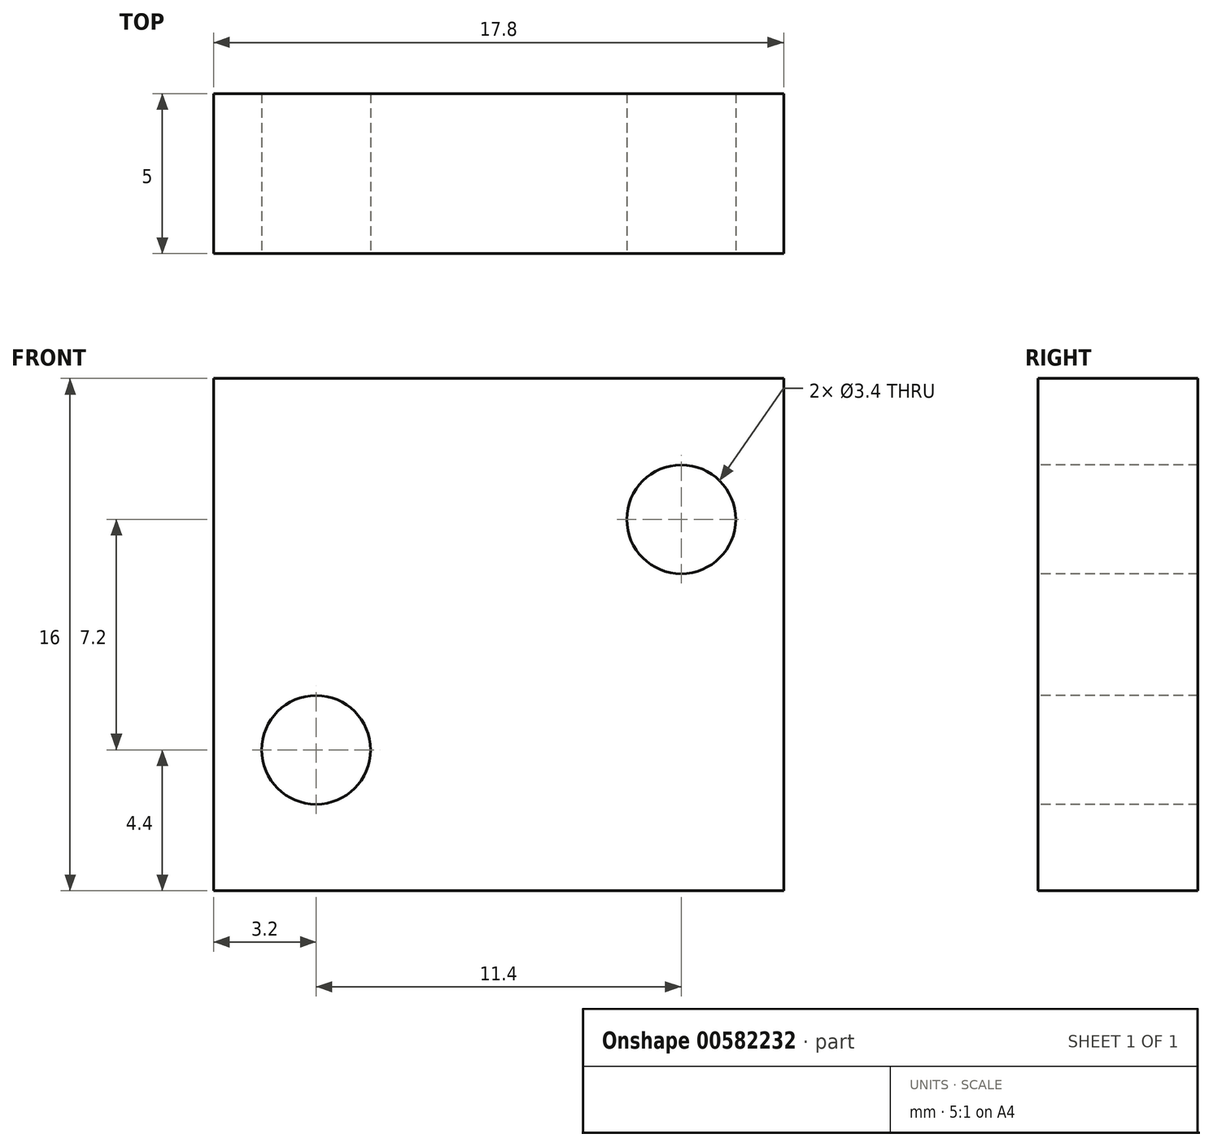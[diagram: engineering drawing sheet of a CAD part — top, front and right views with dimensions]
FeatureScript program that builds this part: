
annotation { "Feature Type Name" : "Feature", "Feature Type Description" : "" }
export const myFeature = defineFeature(function(context is Context, id is Id, definition is map)
    precondition{}
    {
        {
            var Q0;
            Q0=qCreatedBy(makeId("Front.planeOp"),FACE);
            var sketch = newSketch(context, id + "F0", { "sketchPlane" : qUnion([Q0])});
            skLineSegment(sketch, "E0.bottom", {"start": v(0, 0) * mm, "end": v(17.8, 0) * mm});
            skLineSegment(sketch, "E0.top", {"start": v(0, -16) * mm, "end": v(17.8, -16) * mm});
            skLineSegment(sketch, "E0.left", {"start": v(0, 0) * mm, "end": v(0, -16) * mm});
            skLineSegment(sketch, "E0.right", {"start": v(17.8, 0) * mm, "end": v(17.8, -16) * mm});
            skSolve(sketch);
        }
        {
            var Q0;
            Q0=makeQuery(id+"F0.imprint","IMPRINT",FACE,{"disambiguationData":[TD([[makeQuery(id+"F0.imprint","IMPRINT",EDGE,{"derivedFrom":sQuery(id+"F0.wireOp",EDGE,"E0.bottom")}),-1.0]])]});
            extrude(context, id + "F1", {"entities" : qUnion([Q0]), "oppositeDirection" : true, "depth" : 5 * mm, "offsetDistance" : 25 * mm});
        }
        {
            var Q0;
            Q0=makeQuery(id+"F1.opExtrude","CAP_FACE",FACE,{"disambiguationData":[OSD([sQuery(id+"F0.wireOp",EDGE,"E0.bottom"),sQuery(id+"F0.wireOp",EDGE,"E0.top"),sQuery(id+"F0.wireOp",EDGE,"E0.left"),sQuery(id+"F0.wireOp",EDGE,"E0.right")])],"isStart":true});
            var sketch = newSketch(context, id + "F2", { "sketchPlane" : qUnion([Q0])});
            skCircle(sketch, "E1", {"center": v(3.2, -11.6) * mm, "radius": 1.7 * mm});
            skCircle(sketch, "E2", {"center": v(14.6, -4.4) * mm, "radius": 1.7 * mm});
            skSolve(sketch);
        }
        {
            var Q0;
            Q0=makeQuery(id+"F2.imprint","IMPRINT",FACE,{"disambiguationData":[TD([[makeQuery(id+"F2.imprint","IMPRINT",EDGE,{"derivedFrom":sQuery(id+"F2.wireOp",EDGE,"E1")}),1.0]])]});
            var Q1;
            Q1=makeQuery(id+"F2.imprint","IMPRINT",FACE,{"disambiguationData":[TD([[makeQuery(id+"F2.imprint","IMPRINT",EDGE,{"derivedFrom":sQuery(id+"F2.wireOp",EDGE,"E2")}),1.0]])]});
            extrude(context, id + "F3", {"entities" : qUnion([Q0, Q1]), "operationType" : NewBodyOperationType.REMOVE, "endBound" : BoundingType.THROUGH_ALL, "oppositeDirection" : true, "depth" : 25 * mm, "offsetDistance" : 25 * mm});
        }
    });
